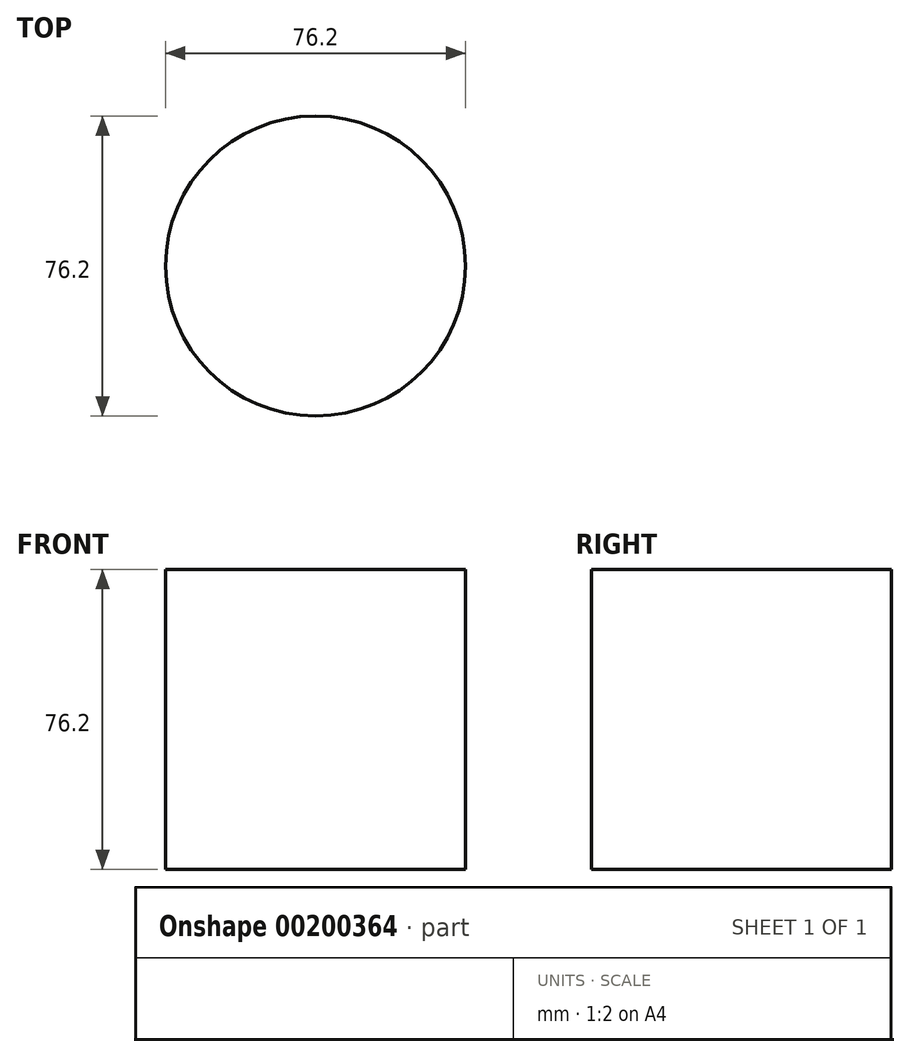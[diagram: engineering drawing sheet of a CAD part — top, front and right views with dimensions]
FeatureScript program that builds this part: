
annotation { "Feature Type Name" : "Feature", "Feature Type Description" : "" }
export const myFeature = defineFeature(function(context is Context, id is Id, definition is map)
    precondition{}
    {
        {
            var Q0;
            Q0=qCreatedBy(makeId("Top.planeOp"),FACE);
            var sketch = newSketch(context, id + "F0", { "sketchPlane" : qUnion([Q0])});
            skCircle(sketch, "E0", {"center": v(0, 0) * mm, "radius": 38.1 * mm});
            skSolve(sketch);
        }
        {
            var Q0;
            Q0 = qSketchRegion(id + "F0", true);
            extrude(context, id + "F1", {"entities" : qUnion([Q0]), "depth" : 76.2 * mm});
        }
    });
